# Revit family: Cluster_Stool_BIM
name_source: partatom
category: Arredi
units: mm (PartAtom-declared; Revit-internal decimal feet)

## family parameters
Attiva taglio nelle viste = No
Basato su piano di lavoro = No
Condiviso = No
Numero OmniClass = 23.40.20.00
Origine composizione di rendering = Geometria famiglia
Punto di calcolo locali = No
Sempre verticale = Sì
Taglio con vuoti quando caricato = No
Titolo OmniClass = General Furniture and Specialties

## types (1)
- CB-122
    AVAILABLE FINISHES = Ebonized black lacquer on Oak (EB). Raw effect lacquer on Oak (RE). Hand rubbed natural oil on Oak or Walnut (NA), or hand rubbed black oil on Walnut (BO).
    BASE MATERIAL = BASSAM_FELLOWS_WALNUT
    BIM BADGE = https://bim.archiproducts.com
    COLLECTION = Cluster
    DEPTH = 400 mm  [stored 1.31234 ft]
    Descrizione = Stackable solid wood stool
    HEIGHT = 43 mm
    MATERIAL DESCRIPTION = Carved solid wood.
    Modello = Cluster Stool
    PRODUCT CODE = CB-122
    PRODUCT SHEET = https://www.archiproducts.com
    Produttore = BassamFellows
    Prospetto di default = 0 mm  [stored 0 ft]
    TECHNICAL SHEET = https://bassamfellows.com
    URL = https://bassamfellows.com
    WEIGHT = 0.00 kg
    WIDTH = 500 mm  [stored 1.64042 ft]

note: [stored X ft] marks values corroborated as IEEE doubles in the binary element streams (Revit-internal decimal feet)

## geometry (parser evidence)
native form markers: Sweep x3
no freeform markers — native parametric forms only
